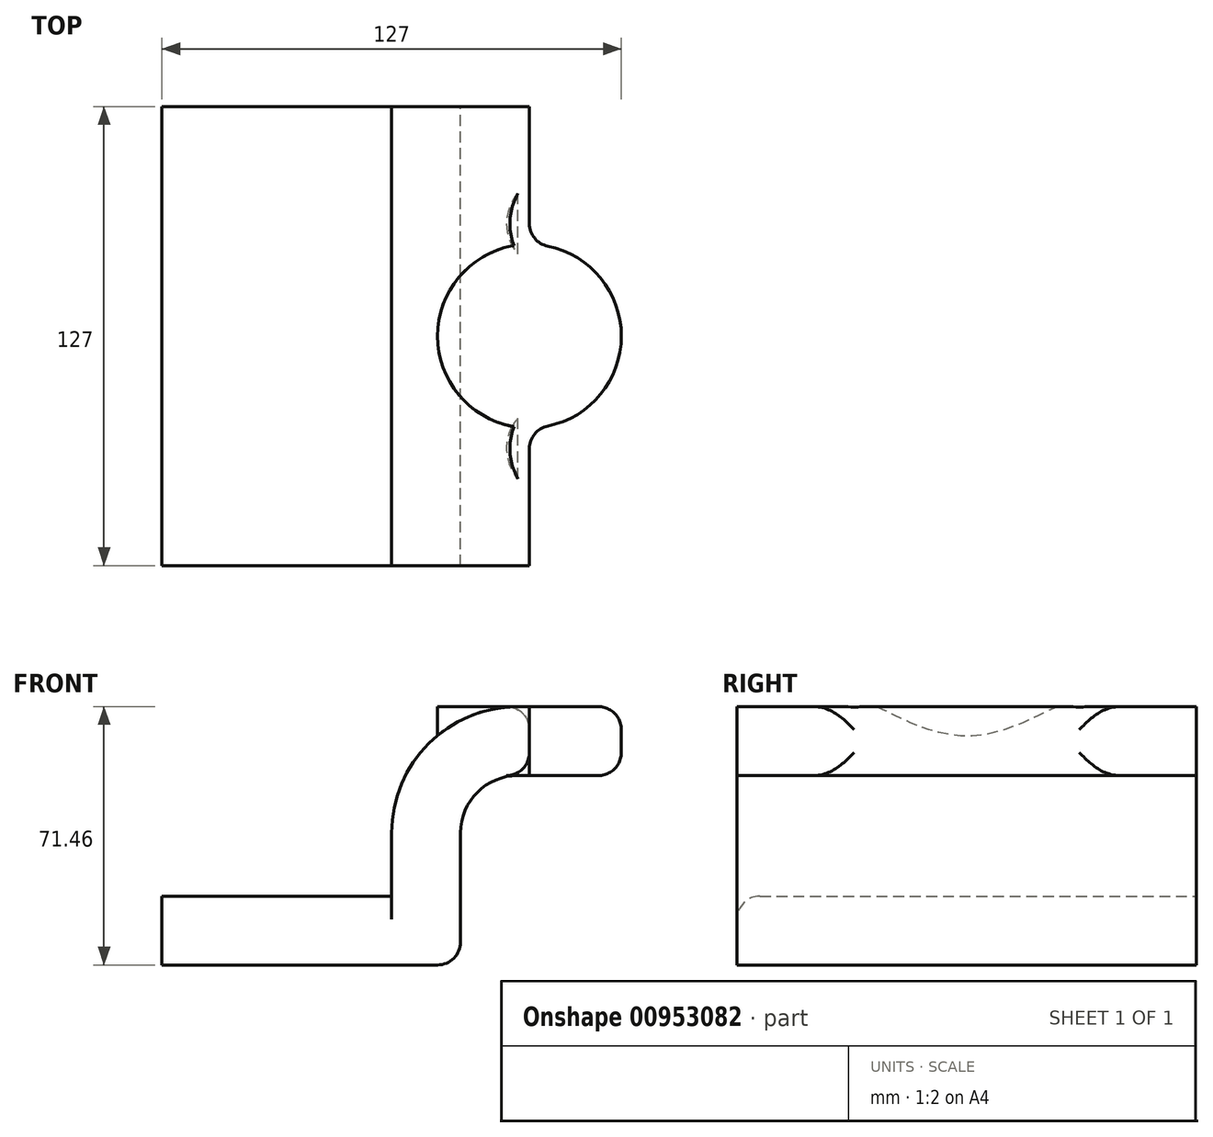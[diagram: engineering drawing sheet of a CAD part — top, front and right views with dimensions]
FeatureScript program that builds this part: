
annotation { "Feature Type Name" : "Feature", "Feature Type Description" : "" }
export const myFeature = defineFeature(function(context is Context, id is Id, definition is map)
    precondition{}
    {
        {
            var Q0;
            Q0=qCreatedBy(makeId("Front.planeOp"),FACE);
            var sketch = newSketch(context, id + "F0", { "sketchPlane" : qUnion([Q0])});
            skLineSegment(sketch, "E0.bottom", {"start": v(41.28, -9.52) * mm, "end": v(-41.28, -9.52) * mm});
            skLineSegment(sketch, "E0.top", {"start": v(41.28, 9.53) * mm, "end": v(-41.28, 9.53) * mm});
            skLineSegment(sketch, "E0.left", {"start": v(41.28, -9.52) * mm, "end": v(41.28, 9.53) * mm});
            skLineSegment(sketch, "E0.right", {"start": v(-41.28, -9.52) * mm, "end": v(-41.28, 9.53) * mm});
            skPoint(sketch, "E0.middle", {"position": v(0, 0) * mm});
            skLineSegment(sketch, "E1.bottom", {"start": v(111.12, 38.1) * mm, "end": v(60.32, 38.1) * mm});
            skLineSegment(sketch, "E1.top", {"start": v(111.12, 66.68) * mm, "end": v(60.32, 66.68) * mm});
            skLineSegment(sketch, "E1.left", {"start": v(111.12, 38.1) * mm, "end": v(111.12, 66.68) * mm});
            skLineSegment(sketch, "E1.right", {"start": v(60.32, 38.1) * mm, "end": v(60.32, 66.67) * mm});
            skPoint(sketch, "E1.middle", {"position": v(85.72, 52.39) * mm});
            skLineSegment(sketch, "E2", {"start": v(41.28, 9.53) * mm, "end": v(41.28, 27) * mm});
            skArc(sketch, "E3", {"start": v(41.27, 27) * mm, "mid": v(45.92, 38.23) * mm, "end": v(57.15, 42.88) * mm});
            skLineSegment(sketch, "E4", {"start": v(57.15, 42.88) * mm, "end": v(85.72, 42.88) * mm});
            skLineSegment(sketch, "E5.0", {"start": v(57.15, 61.93) * mm, "end": v(85.72, 61.93) * mm});
            skArc(sketch, "E5.1", {"start": v(22.23, 27) * mm, "mid": v(32.45, 51.7) * mm, "end": v(57.15, 61.93) * mm});
            skLineSegment(sketch, "E5.2", {"start": v(22.22, 9.53) * mm, "end": v(22.22, 27) * mm});
            skLineSegment(sketch, "E6", {"start": v(85.72, 38.1) * mm, "end": v(85.72, 66.68) * mm});
            skFitSpline(sketch, "E7", {"points": [v(-41.28, 9.52) * mm, v(57.15, 61.93) * mm], "startDerivative": vector(14.13, 96.35) * mm, "endDerivative": vector(149.28, -1.52) * mm});
            skSolve(sketch);
        }
        {
            var Q0;
            Q0=makeQuery(id+"F0.imprint","IMPRINT",FACE,{"disambiguationData":[TD([[makeQuery(id+"F0.imprint","IMPRINT",EDGE,{"derivedFrom":sQuery(id+"F0.wireOp",EDGE,"E0.bottom")}),-1.0]])]});
            extrude(context, id + "F1", {"entities" : qUnion([Q0]), "endBound" : BoundingType.SYMMETRIC, "depth" : 127 * mm, "offsetDistance" : 25.4 * mm});
        }
        {
            var Q0;
            {var subQ1=sQuery(id+"F0.wireOp",EDGE,"E2");Q0=makeQuery(id+"F0.imprint","IMPRINT",FACE,{"disambiguationData":[TD([[makeQuery(id+"F0.imprint","IMPRINT",EDGE,{"derivedFrom":subQ1}),1.0]])]});}
            extrude(context, id + "F2", {"entities" : qUnion([Q0]), "operationType" : NewBodyOperationType.ADD, "endBound" : BoundingType.SYMMETRIC, "depth" : 127 * mm, "offsetDistance" : 25.4 * mm});
        }
        {
            var Q0;
            Q0=makeQuery(id+"F0.imprint","IMPRINT",FACE,{"disambiguationData":[TD([[makeQuery(id+"F0.imprint","IMPRINT",EDGE,{"derivedFrom":sQuery(id+"F0.wireOp",EDGE,"E5.1")}),1.0]])]});
            extrude(context, id + "F3", {"entities" : qUnion([Q0]), "operationType" : NewBodyOperationType.ADD, "endBound" : BoundingType.SYMMETRIC, "depth" : 17.14 * mm, "offsetDistance" : 25.4 * mm});
        }
        {
            var Q0;
            {var subQ0=sQuery(id+"F0.wireOp",EDGE,"E4");var subQ1=sQuery(id+"F0.wireOp",EDGE,"E1.right");var subQ2=makeQuery(id+"F0.imprint","INTERSECT",VERTEX,{"derivedFrom":[subQ1,subQ0]});Q0=makeQuery(id+"F0.imprint","IMPRINT",FACE,{"disambiguationData":[TD([[makeQuery(id+"F0.imprint","IMPRINT",EDGE,{"disambiguationData":[TD([[subQ2,-1.0]])],"derivedFrom":subQ1}),-1.0]])]});}
            var Q1;
            Q1=sQuery(id+"F0.wireOp",EDGE,"E1.right");
            revolve(context, id + "F4", {"operationType" : NewBodyOperationType.ADD, "surfaceOperationType" : NewSurfaceOperationType.NEW, "entities" : qUnion([Q0]), "axis" : qUnion([Q1]), "revolveType" : RevolveType.FULL});
        }
        {
            var Q0;
            Q0=makeQuery(id+"F1.opExtrude","CAP_EDGE",EDGE,{"disambiguationData":[OSD([sQuery(id+"F0.wireOp",EDGE,"E0.top")])],"isStart":false});
            var Q1;
            Q1=makeQuery(id+"F4.boolean.opBoolean","SPLIT",FACE,{"disambiguationData":[TD([makeQuery(id+"F2.opExtrude","SWEPT_FACE",FACE,{"disambiguationData":[OSD([sQuery(id+"F0.wireOp",EDGE,"E1.right")])]})])],"derivedFrom":makeQuery(id+"F4.opRevolve","SWEPT_FACE",FACE,{"disambiguationData":[OSD([sQuery(id+"F0.wireOp",EDGE,"E6")])]})});
            var Q2;
            Q2=makeQuery(id+"F1.opExtrude","SWEPT_EDGE",EDGE,{"disambiguationData":[OSD([sQuery(id+"F0.wireOp",EDGE,"E0.bottom"),sQuery(id+"F0.wireOp",EDGE,"E0.left")])]});
            var Q3;
            {var subQ0=sQuery(id+"F0.wireOp",EDGE,"E7");var subQ1=sQuery(id+"F0.wireOp",EDGE,"E0.top");Q3=makeQuery(id+"F4.boolean.opBoolean","SPLIT",EDGE,{"disambiguationData":[TD([makeQuery(id+"F1.opExtrude","SWEPT_FACE",FACE,{"disambiguationData":[OSD([subQ1])]})])],"derivedFrom":makeQuery(id+"F3.opExtrude","CAP_EDGE",EDGE,{"disambiguationData":[OSD([subQ0])],"isStart":true})});}
            fillet(context, id + "F5", {"entities" : qUnion([Q0, Q1, Q2, Q3]), "radius" : 6.35 * mm, "tangentPropagation" : true, "allowEdgeOverflow" : false});
        }
    });
